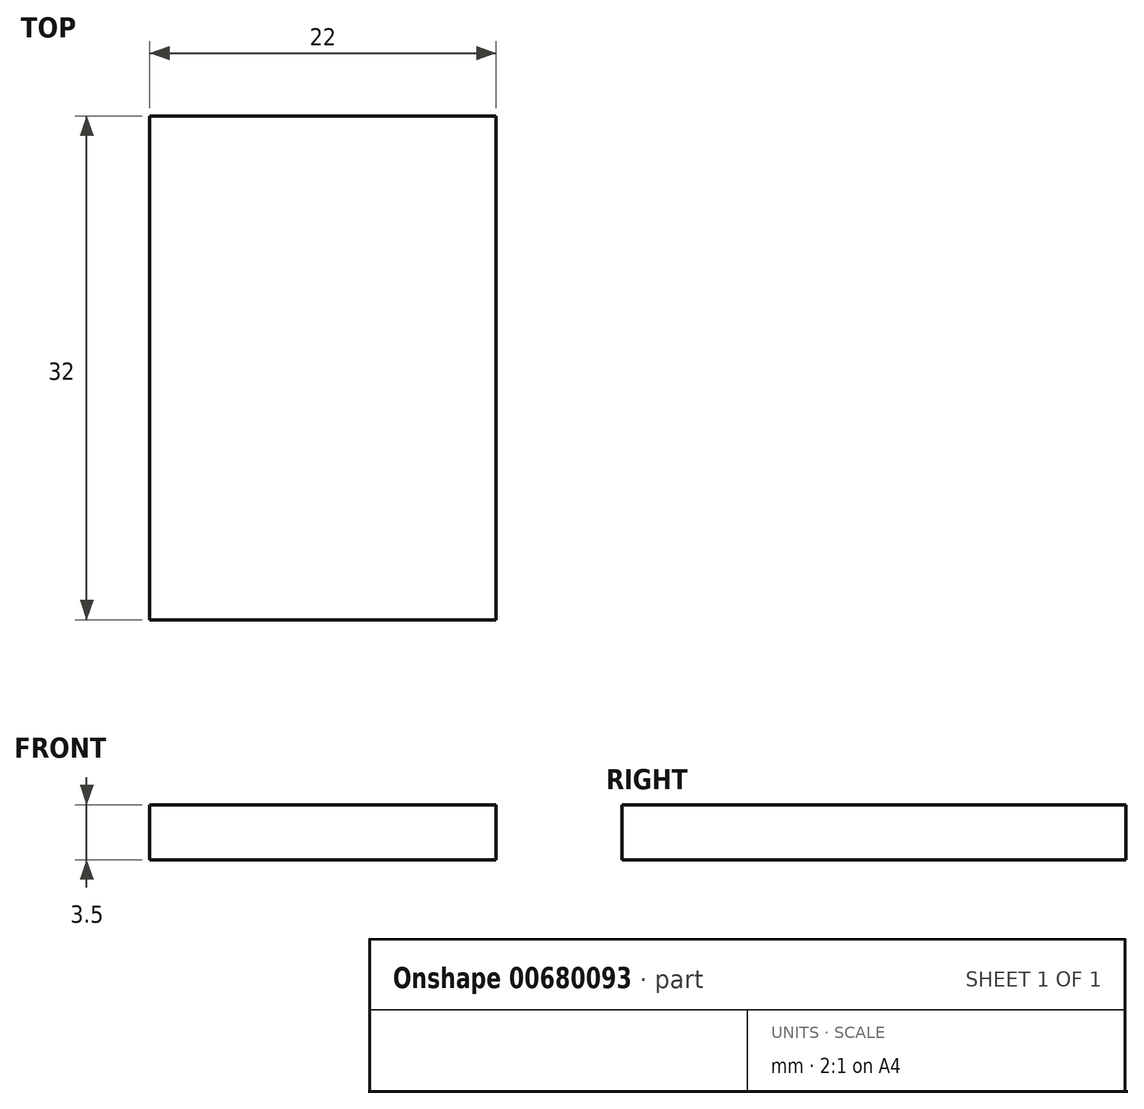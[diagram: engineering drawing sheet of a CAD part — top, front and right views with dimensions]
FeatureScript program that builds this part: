
annotation { "Feature Type Name" : "Feature", "Feature Type Description" : "" }
export const myFeature = defineFeature(function(context is Context, id is Id, definition is map)
    precondition{}
    {
        {
            var Q0;
            Q0=qCreatedBy(makeId("Top.planeOp"),FACE);
            var sketch = newSketch(context, id + "F0", { "sketchPlane" : qUnion([Q0])});
            skLineSegment(sketch, "E0.bottom", {"start": v(11, -16) * mm, "end": v(-11, -16) * mm});
            skLineSegment(sketch, "E0.top", {"start": v(11, 16) * mm, "end": v(-11, 16) * mm});
            skLineSegment(sketch, "E0.left", {"start": v(11, -16) * mm, "end": v(11, 16) * mm});
            skLineSegment(sketch, "E0.right", {"start": v(-11, -16) * mm, "end": v(-11, 16) * mm});
            skPoint(sketch, "E0.middle", {"position": v(0, 0) * mm});
            skSolve(sketch);
        }
        {
            var Q0;
            Q0=makeQuery(id+"F0.imprint","IMPRINT",FACE,{"disambiguationData":[TD([[makeQuery(id+"F0.imprint","IMPRINT",EDGE,{"derivedFrom":sQuery(id+"F0.wireOp",EDGE,"E0.bottom")}),-1.0]])]});
            extrude(context, id + "F1", {"entities" : qUnion([Q0]), "depth" : 3.5 * mm, "offsetDistance" : 25.4 * mm, "symmetric" : true});
        }
    });
